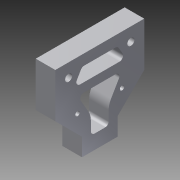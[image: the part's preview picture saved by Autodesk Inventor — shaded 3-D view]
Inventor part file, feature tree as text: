
AUTODESK INVENTOR PART (.ipt)
format: ipt  version: 2013 (Build 170138000, 138)  size: 246,272 bytes
history: native  units: mm
features: sketch x8, extrude x6, hole x2, fillet x2, other x1, pattern_circular x1
ambient origin geometry x8: Origin, YZ Plane, XZ Plane, XY Plane, X Axis, Y Axis, Z Axis, Center Point
feature tree (20):
  other  "ソリッド1"
  extrude  "押し出し1"  Depth=100.0mm
  extrude  "押し出し2"  Depth=100.0mm
  extrude  "押し出し5"  Depth=50.0mm
  hole  "穴1"  [1 undecoded]
  pattern_circular  "円形状パターン2"  [2 undecoded]
  hole  "穴2"  [1 undecoded]
  extrude  "押し出し6"  TaperAngle=135.0deg  [1 undecoded]
  sketch  "スケッチ7"
  sketch  "スケッチ8"
  extrude  "押し出し11"  Depth=25.0mm
  extrude  "押し出し12"  Depth=25.0mm
  fillet  "フィレット1"  Radius=50.0mm
  fillet  "フィレット2"  [1 undecoded]
  sketch  "スケッチ1"
  sketch  "スケッチ2"
  sketch  "スケッチ3"
  sketch  "スケッチ4"
  sketch  "スケッチ5"
  sketch  "スケッチ6"
note: 6 required parameter values undecoded (feature->parameter linkage not recoverable at this tier; creation-order binding heuristic only, values carry confidence <= 0.55)
